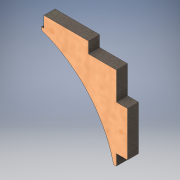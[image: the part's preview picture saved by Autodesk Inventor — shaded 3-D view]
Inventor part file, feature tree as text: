
AUTODESK INVENTOR PART (.ipt)
format: ipt  version: 2019 (Build 230136000, 136)  size: 126,976 bytes
history: native  units: mm
features: other x1, extrude x1, sketch x1
ambient origin geometry x8: Origin, YZ Plane, XZ Plane, XY Plane, X Axis, Y Axis, Z Axis, Center Point
bodies: Body1 (feature_tree)
feature tree (3):
  other  "Твердое тело1"
  extrude  "Выдавливание1"  Depth=40.0mm
  sketch  "Эскиз1"
